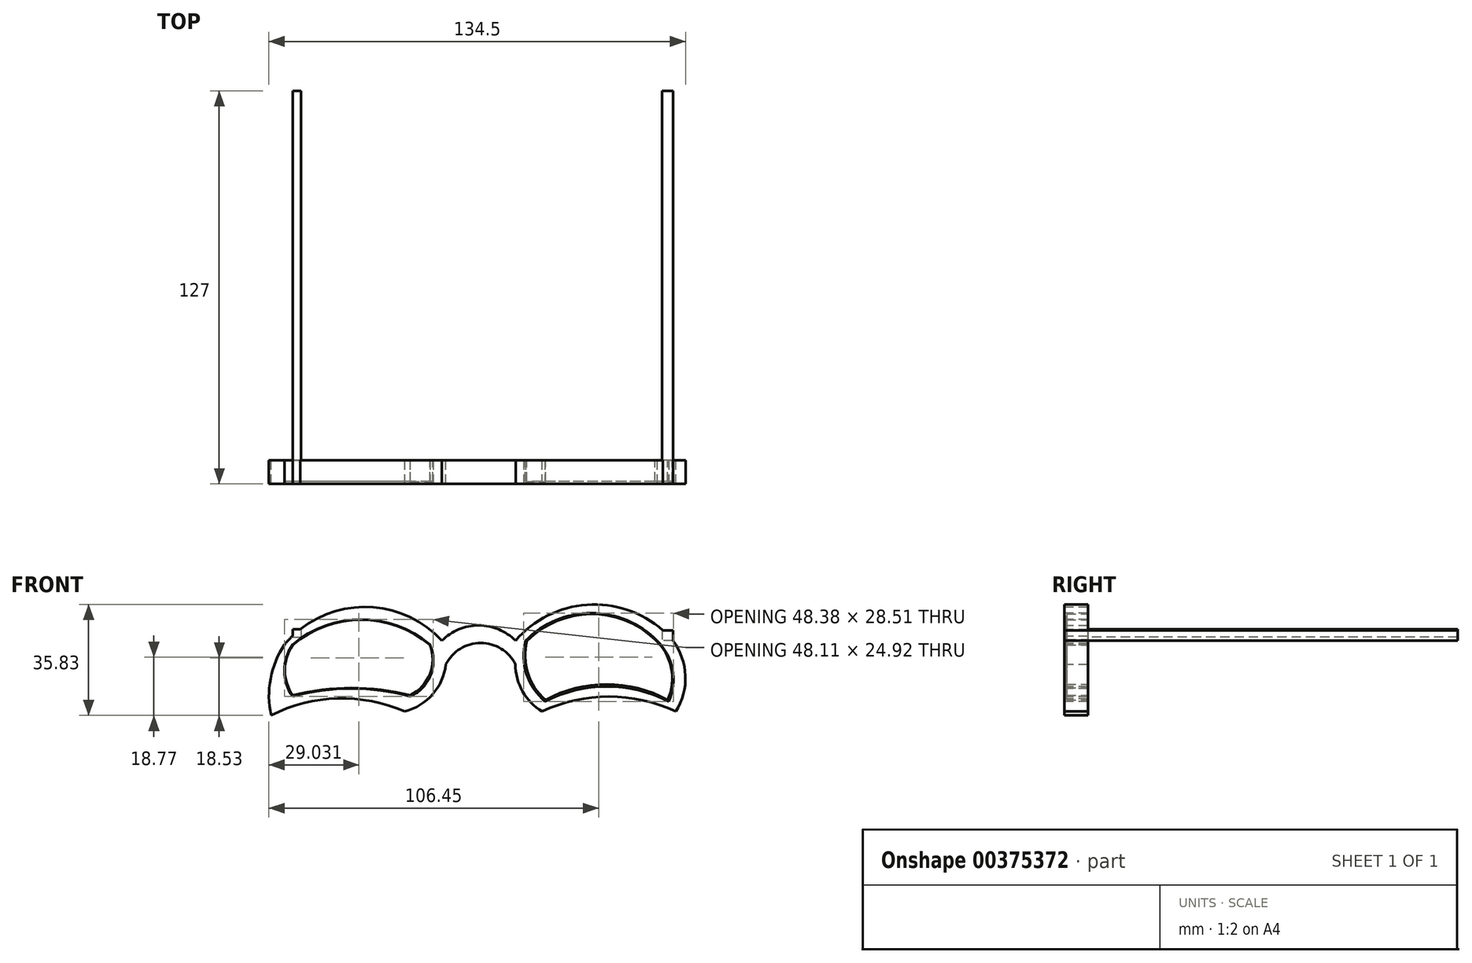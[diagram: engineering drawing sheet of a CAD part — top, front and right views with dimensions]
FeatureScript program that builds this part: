
annotation { "Feature Type Name" : "Feature", "Feature Type Description" : "" }
export const myFeature = defineFeature(function(context is Context, id is Id, definition is map)
    precondition{}
    {
        {
            var Q0;
            Q0=qCreatedBy(makeId("Front.planeOp"),FACE);
            var sketch = newSketch(context, id + "F0", { "sketchPlane" : qUnion([Q0])});
            skArc(sketch, "E0", {"start": v(0.86, 8.96) * mm, "mid": v(-11.06, 13.92) * mm, "end": v(-22.98, 8.96) * mm});
            skArc(sketch, "E1", {"start": v(0.8, 1.34) * mm, "mid": v(-10.41, 8.24) * mm, "end": v(-21.63, 1.34) * mm});
            skArc(sketch, "E2", {"start": v(-22.98, 8.96) * mm, "mid": v(-48.67, 19.86) * mm, "end": v(-73.78, 7.7) * mm});
            skArc(sketch, "E3", {"start": v(51.66, 8.96) * mm, "mid": v(26.26, 20.67) * mm, "end": v(0.86, 8.96) * mm});
            skArc(sketch, "E4", {"start": v(-34.93, -13.9) * mm, "mid": v(-56.66, -9.7) * mm, "end": v(-78.1, -15.16) * mm});
            skArc(sketch, "E5", {"start": v(-34.93, -13.9) * mm, "mid": v(-25.92, -8.33) * mm, "end": v(-21.63, 1.34) * mm});
            skArc(sketch, "E6", {"start": v(0.8, 1.34) * mm, "mid": v(3.11, -7.4) * mm, "end": v(9.4, -13.9) * mm});
            skArc(sketch, "E7", {"start": v(52.57, -13.9) * mm, "mid": v(30.98, -9.08) * mm, "end": v(9.4, -13.9) * mm});
            skArc(sketch, "E8", {"start": v(52.57, -13.9) * mm, "mid": v(55.7, -2.32) * mm, "end": v(51.66, 8.96) * mm});
            skArc(sketch, "E9", {"start": v(-73.78, 7.7) * mm, "mid": v(-78.27, -3.3) * mm, "end": v(-78.1, -15.16) * mm});
            skSolve(sketch);
        }
        {
            var Q0;
            Q0 = qSketchRegion(id + "F0", true);
            extrude(context, id + "F1", {"entities" : qUnion([Q0]), "depth" : 7.62 * mm});
        }
        {
            var Q0;
            Q0=makeQuery(id+"F1.opExtrude","CAP_FACE",FACE,{"disambiguationData":[OSD([sQuery(id+"F0.wireOp",EDGE,"E0"),sQuery(id+"F0.wireOp",EDGE,"E1"),sQuery(id+"F0.wireOp",EDGE,"E2"),sQuery(id+"F0.wireOp",EDGE,"E3"),sQuery(id+"F0.wireOp",EDGE,"E4"),sQuery(id+"F0.wireOp",EDGE,"E5"),sQuery(id+"F0.wireOp",EDGE,"E6"),sQuery(id+"F0.wireOp",EDGE,"E7"),sQuery(id+"F0.wireOp",EDGE,"E8"),sQuery(id+"F0.wireOp",EDGE,"E9")])],"isStart":false});
            var sketch = newSketch(context, id + "F2", { "sketchPlane" : qUnion([Q0])});
            skLineSegment(sketch, "E10.bottom", {"start": v(51.65, 12.32) * mm, "end": v(48.15, 12.32) * mm});
            skLineSegment(sketch, "E10.top", {"start": v(51.65, 8.98) * mm, "end": v(48.15, 8.98) * mm});
            skLineSegment(sketch, "E10.left", {"start": v(51.65, 12.32) * mm, "end": v(51.65, 8.98) * mm});
            skLineSegment(sketch, "E10.right", {"start": v(48.15, 12.32) * mm, "end": v(48.15, 8.98) * mm});
            skSolve(sketch);
        }
        {
            var Q0;
            Q0 = qSketchRegion(id + "F2", true);
            extrude(context, id + "F3", {"entities" : qUnion([Q0]), "operationType" : NewBodyOperationType.REMOVE, "oppositeDirection" : true, "depth" : 25.4 * mm});
        }
        {
            var Q0;
            Q0=makeQuery(id+"F1.opExtrude","CAP_FACE",FACE,{"disambiguationData":[OSD([sQuery(id+"F0.wireOp",EDGE,"E0"),sQuery(id+"F0.wireOp",EDGE,"E1"),sQuery(id+"F0.wireOp",EDGE,"E2"),sQuery(id+"F0.wireOp",EDGE,"E3"),sQuery(id+"F0.wireOp",EDGE,"E4"),sQuery(id+"F0.wireOp",EDGE,"E5"),sQuery(id+"F0.wireOp",EDGE,"E6"),sQuery(id+"F0.wireOp",EDGE,"E7"),sQuery(id+"F0.wireOp",EDGE,"E8"),sQuery(id+"F0.wireOp",EDGE,"E9")])],"isStart":false});
            var sketch = newSketch(context, id + "F4", { "sketchPlane" : qUnion([Q0])});
            skLineSegment(sketch, "E11.bottom", {"start": v(-71.13, 12.66) * mm, "end": v(-68.48, 12.66) * mm});
            skLineSegment(sketch, "E11.top", {"start": v(-71.13, 10.1) * mm, "end": v(-68.48, 10.1) * mm});
            skLineSegment(sketch, "E11.left", {"start": v(-71.13, 12.66) * mm, "end": v(-71.13, 10.1) * mm});
            skLineSegment(sketch, "E11.right", {"start": v(-68.48, 12.66) * mm, "end": v(-68.48, 10.1) * mm});
            skSolve(sketch);
        }
        {
            var Q0;
            Q0 = qSketchRegion(id + "F4", true);
            extrude(context, id + "F5", {"entities" : qUnion([Q0]), "operationType" : NewBodyOperationType.REMOVE, "oppositeDirection" : true, "depth" : 25.4 * mm});
        }
        {
            var Q0;
            Q0=makeQuery(id+"F1.opExtrude","CAP_FACE",FACE,{"disambiguationData":[OSD([sQuery(id+"F0.wireOp",EDGE,"E0"),sQuery(id+"F0.wireOp",EDGE,"E1"),sQuery(id+"F0.wireOp",EDGE,"E2"),sQuery(id+"F0.wireOp",EDGE,"E3"),sQuery(id+"F0.wireOp",EDGE,"E4"),sQuery(id+"F0.wireOp",EDGE,"E5"),sQuery(id+"F0.wireOp",EDGE,"E6"),sQuery(id+"F0.wireOp",EDGE,"E7"),sQuery(id+"F0.wireOp",EDGE,"E8"),sQuery(id+"F0.wireOp",EDGE,"E9")])],"isStart":false});
            var sketch = newSketch(context, id + "F6", { "sketchPlane" : qUnion([Q0])});
            skLineSegment(sketch, "E12.bottom", {"start": v(-68.48, 12.66) * mm, "end": v(-71.13, 12.66) * mm});
            skLineSegment(sketch, "E12.top", {"start": v(-68.48, 10.1) * mm, "end": v(-71.13, 10.1) * mm});
            skLineSegment(sketch, "E12.left", {"start": v(-68.48, 12.66) * mm, "end": v(-68.48, 10.1) * mm});
            skLineSegment(sketch, "E12.right", {"start": v(-71.13, 12.66) * mm, "end": v(-71.13, 10.1) * mm});
            skSolve(sketch);
        }
        {
            var Q0;
            Q0=makeQuery(id+"FpkjilLXlsyoWuy_1.boolean.opBoolean","MERGE",FACE,{"derivedFrom":[makeQuery(id+"F1.opExtrude","CAP_FACE",FACE,{"disambiguationData":[OSD([sQuery(id+"F0.wireOp",EDGE,"E0"),sQuery(id+"F0.wireOp",EDGE,"E1"),sQuery(id+"F0.wireOp",EDGE,"E2"),sQuery(id+"F0.wireOp",EDGE,"E3"),sQuery(id+"F0.wireOp",EDGE,"E4"),sQuery(id+"F0.wireOp",EDGE,"E5"),sQuery(id+"F0.wireOp",EDGE,"E6"),sQuery(id+"F0.wireOp",EDGE,"E7"),sQuery(id+"F0.wireOp",EDGE,"E8"),sQuery(id+"F0.wireOp",EDGE,"E9")])],"isStart":false}),makeQuery(id+"FpkjilLXlsyoWuy_1.opExtrude","CAP_FACE",FACE,{"disambiguationData":[OSD([sQuery(id+"F6.wireOp",EDGE,"E12.bottom"),sQuery(id+"F6.wireOp",EDGE,"E12.top"),sQuery(id+"F6.wireOp",EDGE,"E12.left"),sQuery(id+"F6.wireOp",EDGE,"E12.right")])],"isStart":true})]});
            var sketch = newSketch(context, id + "F7", { "sketchPlane" : qUnion([Q0])});
            skLineSegment(sketch, "E13.bottom", {"start": v(48.15, 12.32) * mm, "end": v(51.65, 12.32) * mm});
            skLineSegment(sketch, "E13.top", {"start": v(48.15, 8.98) * mm, "end": v(51.65, 8.98) * mm});
            skLineSegment(sketch, "E13.left", {"start": v(48.15, 12.32) * mm, "end": v(48.15, 8.98) * mm});
            skLineSegment(sketch, "E13.right", {"start": v(51.65, 12.32) * mm, "end": v(51.65, 8.98) * mm});
            skSolve(sketch);
        }
        {
            var Q0;
            Q0=makeQuery(id+"FpkjilLXlsyoWuy_1.boolean.opBoolean","MERGE",FACE,{"derivedFrom":[makeQuery(id+"F1.opExtrude","CAP_FACE",FACE,{"disambiguationData":[OSD([sQuery(id+"F0.wireOp",EDGE,"E0"),sQuery(id+"F0.wireOp",EDGE,"E1"),sQuery(id+"F0.wireOp",EDGE,"E2"),sQuery(id+"F0.wireOp",EDGE,"E3"),sQuery(id+"F0.wireOp",EDGE,"E4"),sQuery(id+"F0.wireOp",EDGE,"E5"),sQuery(id+"F0.wireOp",EDGE,"E6"),sQuery(id+"F0.wireOp",EDGE,"E7"),sQuery(id+"F0.wireOp",EDGE,"E8"),sQuery(id+"F0.wireOp",EDGE,"E9")])],"isStart":false}),makeQuery(id+"FpkjilLXlsyoWuy_1.opExtrude","CAP_FACE",FACE,{"disambiguationData":[OSD([sQuery(id+"F6.wireOp",EDGE,"E12.bottom"),sQuery(id+"F6.wireOp",EDGE,"E12.top"),sQuery(id+"F6.wireOp",EDGE,"E12.left"),sQuery(id+"F6.wireOp",EDGE,"E12.right")])],"isStart":true})]});
            var sketch = newSketch(context, id + "F8", { "sketchPlane" : qUnion([Q0])});
            skArc(sketch, "E14", {"start": v(-26.83, 7.7) * mm, "mid": v(-48.98, 15.83) * mm, "end": v(-71.13, 7.7) * mm});
            skArc(sketch, "E15", {"start": v(-71.13, 7.7) * mm, "mid": v(-73.81, -0.7) * mm, "end": v(-71.13, -9.1) * mm});
            skArc(sketch, "E16", {"start": v(-33.2, -9.1) * mm, "mid": v(-52.17, -6.47) * mm, "end": v(-71.13, -9.1) * mm});
            skArc(sketch, "E17", {"start": v(-33.2, -9.1) * mm, "mid": v(-26.52, -2.02) * mm, "end": v(-26.83, 7.7) * mm});
            skSolve(sketch);
        }
        {
            var Q0;
            Q0 = qSketchRegion(id + "F8", true);
            extrude(context, id + "F9", {"entities" : qUnion([Q0]), "operationType" : NewBodyOperationType.REMOVE, "oppositeDirection" : true, "depth" : 25.4 * mm});
        }
        {
            var Q0;
            Q0=makeQuery(id+"F0.imprint","IMPRINT",FACE,{"disambiguationData":[TD([[makeQuery(id+"F0.imprint","IMPRINT",EDGE,{"derivedFrom":sQuery(id+"F0.wireOp",EDGE,"E0")}),1.0]])]});
            var sketch = newSketch(context, id + "F10", { "sketchPlane" : qUnion([Q0])});
            skArc(sketch, "E18", {"start": v(-26.8, 7.6) * mm, "mid": v(-48.96, 15.67) * mm, "end": v(-71.1, 7.55) * mm});
            skArc(sketch, "E19", {"start": v(-71.1, 7.55) * mm, "mid": v(-73.63, -0.57) * mm, "end": v(-71.1, -8.69) * mm});
            skArc(sketch, "E20", {"start": v(-33.15, -8.69) * mm, "mid": v(-52.12, -6.3) * mm, "end": v(-71.1, -8.69) * mm});
            skArc(sketch, "E21", {"start": v(-33.15, -8.69) * mm, "mid": v(-26.82, -1.77) * mm, "end": v(-26.8, 7.6) * mm});
            skSolve(sketch);
        }
        {
            var Q0;
            Q0 = qSketchRegion(id + "F10", true);
            extrude(context, id + "F11", {"entities" : qUnion([Q0]), "depth" : 6.86 * mm});
        }
        {
            var Q0;
            Q0=makeQuery(id+"FpkjilLXlsyoWuy_1.boolean.opBoolean","MERGE",FACE,{"derivedFrom":[makeQuery(id+"F1.opExtrude","CAP_FACE",FACE,{"disambiguationData":[OSD([sQuery(id+"F0.wireOp",EDGE,"E0"),sQuery(id+"F0.wireOp",EDGE,"E1"),sQuery(id+"F0.wireOp",EDGE,"E2"),sQuery(id+"F0.wireOp",EDGE,"E3"),sQuery(id+"F0.wireOp",EDGE,"E4"),sQuery(id+"F0.wireOp",EDGE,"E5"),sQuery(id+"F0.wireOp",EDGE,"E6"),sQuery(id+"F0.wireOp",EDGE,"E7"),sQuery(id+"F0.wireOp",EDGE,"E8"),sQuery(id+"F0.wireOp",EDGE,"E9")])],"isStart":false}),makeQuery(id+"FpkjilLXlsyoWuy_1.opExtrude","CAP_FACE",FACE,{"disambiguationData":[OSD([sQuery(id+"F6.wireOp",EDGE,"E12.bottom"),sQuery(id+"F6.wireOp",EDGE,"E12.top"),sQuery(id+"F6.wireOp",EDGE,"E12.left"),sQuery(id+"F6.wireOp",EDGE,"E12.right")])],"isStart":true})]});
            var sketch = newSketch(context, id + "F12", { "sketchPlane" : qUnion([Q0])});
            skArc(sketch, "E22", {"start": v(46.5, 8.96) * mm, "mid": v(25.3, 17.86) * mm, "end": v(4.1, 8.96) * mm});
            skArc(sketch, "E23", {"start": v(4.1, 8.96) * mm, "mid": v(4.37, -1.75) * mm, "end": v(10.35, -10.64) * mm});
            skArc(sketch, "E24", {"start": v(50.3, -10.64) * mm, "mid": v(30.33, -5.84) * mm, "end": v(10.35, -10.64) * mm});
            skArc(sketch, "E25", {"start": v(50.3, -10.64) * mm, "mid": v(51.55, -0.23) * mm, "end": v(46.5, 8.96) * mm});
            skSolve(sketch);
        }
        {
            var Q0;
            Q0 = qSketchRegion(id + "F12", true);
            extrude(context, id + "F13", {"entities" : qUnion([Q0]), "operationType" : NewBodyOperationType.REMOVE, "oppositeDirection" : true, "depth" : 25.4 * mm});
        }
        {
            var Q0;
            Q0=makeQuery(id+"F0.imprint","IMPRINT",FACE,{"disambiguationData":[TD([[makeQuery(id+"F0.imprint","IMPRINT",EDGE,{"derivedFrom":sQuery(id+"F0.wireOp",EDGE,"E0")}),1.0]])]});
            var sketch = newSketch(context, id + "F14", { "sketchPlane" : qUnion([Q0])});
            skArc(sketch, "E26", {"start": v(45.89, 9.34) * mm, "mid": v(25.1, 17.58) * mm, "end": v(4.5, 8.85) * mm});
            skArc(sketch, "E27", {"start": v(4.5, 8.85) * mm, "mid": v(4.82, -1.51) * mm, "end": v(10.51, -10.18) * mm});
            skArc(sketch, "E28", {"start": v(50, -10.18) * mm, "mid": v(30.25, -5.12) * mm, "end": v(10.51, -10.18) * mm});
            skArc(sketch, "E29", {"start": v(50, -10.18) * mm, "mid": v(51.09, 0.24) * mm, "end": v(45.89, 9.34) * mm});
            skSolve(sketch);
        }
        {
            var Q0;
            Q0 = qSketchRegion(id + "F14", true);
            extrude(context, id + "F15", {"entities" : qUnion([Q0]), "depth" : 6.86 * mm});
        }
        {
            var Q0;
            Q0=makeQuery(id+"F7.imprint","IMPRINT",FACE,{"disambiguationData":[TD([[makeQuery(id+"F7.imprint","IMPRINT",EDGE,{"derivedFrom":sQuery(id+"F7.wireOp",EDGE,"E13.top")}),-1.0]])]});
            var Q1;
            {var subQ1=sQuery(id+"F6.wireOp",EDGE,"E12.top");Q1=makeQuery(id+"F6.imprint","IMPRINT",FACE,{"disambiguationData":[TD([[makeQuery(id+"F6.imprint","IMPRINT",EDGE,{"derivedFrom":subQ1}),1.0]])]});}
            extrude(context, id + "F16", {"entities" : qUnion([Q0, Q1]), "operationType" : NewBodyOperationType.ADD, "oppositeDirection" : true, "depth" : 127 * mm});
        }
    });
